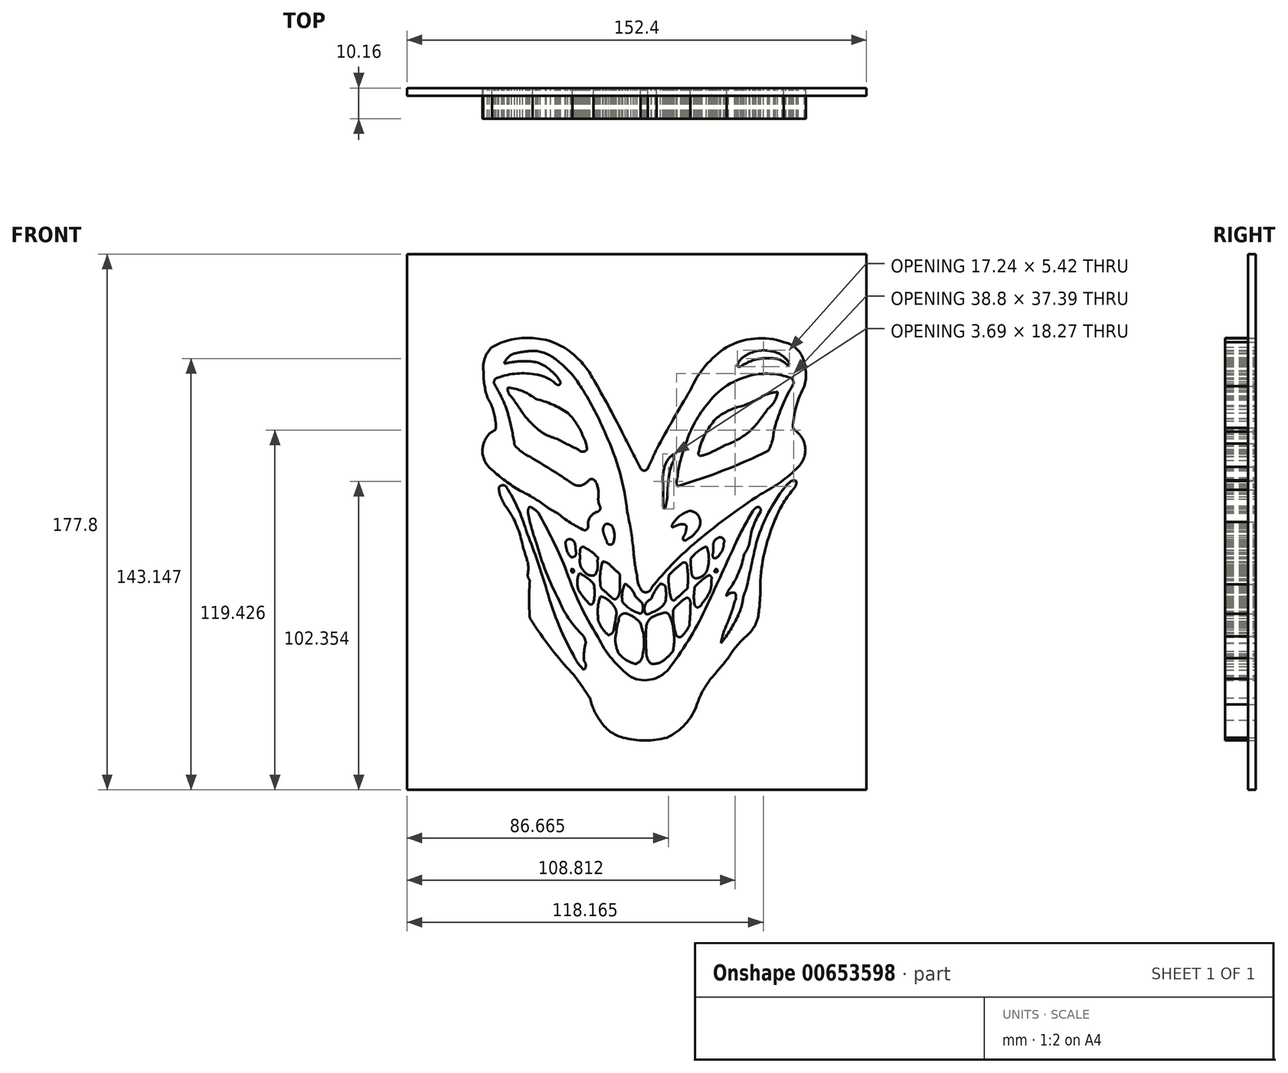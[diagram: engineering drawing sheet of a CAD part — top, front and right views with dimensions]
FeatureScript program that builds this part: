
annotation { "Feature Type Name" : "Feature", "Feature Type Description" : "" }
export const myFeature = defineFeature(function(context is Context, id is Id, definition is map)
    precondition{}
    {
        {
            var Q0;
            Q0=qCreatedBy(makeId("Front.planeOp"),FACE);
            var sketch = newSketch(context, id + "F0", { "sketchPlane" : qUnion([Q0])});
            skArc(sketch, "E0", {"start": v(-41.53, -5.05) * mm, "mid": v(-43.41, 1.4) * mm, "end": v(-46.62, 7.33) * mm});
            skArc(sketch, "E1", {"start": v(-48.45, 10.4) * mm, "mid": v(-47.67, 8.78) * mm, "end": v(-46.62, 7.33) * mm});
            skArc(sketch, "E2", {"start": v(-49.37, 14.24) * mm, "mid": v(-49.18, 12.26) * mm, "end": v(-48.45, 10.4) * mm});
            skArc(sketch, "E3", {"start": v(-46.78, 14.24) * mm, "mid": v(-48.07, 14.96) * mm, "end": v(-49.37, 14.24) * mm});
            skArc(sketch, "E4", {"start": v(-40.37, 0) * mm, "mid": v(-43.1, 7.34) * mm, "end": v(-46.78, 14.24) * mm});
            skArc(sketch, "E5", {"start": v(-33.87, -18.5) * mm, "mid": v(-36.95, -9.2) * mm, "end": v(-40.37, 0) * mm});
            skArc(sketch, "E6", {"start": v(-33.87, -18.5) * mm, "mid": v(-29.97, -30.28) * mm, "end": v(-24.64, -41.48) * mm});
            skArc(sketch, "E7", {"start": v(-24.64, -41.48) * mm, "mid": v(-23.16, -44.1) * mm, "end": v(-21.16, -46.36) * mm});
            skArc(sketch, "E8", {"start": v(-21.16, -46.36) * mm, "mid": v(-20.57, -44.83) * mm, "end": v(-21.16, -43.3) * mm});
            skArc(sketch, "E9", {"start": v(-20.57, -37.35) * mm, "mid": v(-21.1, -40.3) * mm, "end": v(-21.16, -43.3) * mm});
            skPoint(sketch, "E9.startSnap0", {"position": v(-20.57, -44.83) * mm});
            skArc(sketch, "E10", {"start": v(-20.57, -37.35) * mm, "mid": v(-21.1, -35.6) * mm, "end": v(-22.25, -34.18) * mm});
            skArc(sketch, "E11", {"start": v(-29.38, -23.38) * mm, "mid": v(-26.34, -29.12) * mm, "end": v(-22.25, -34.18) * mm});
            skArc(sketch, "E12", {"start": v(-37.08, -3.88) * mm, "mid": v(-33.77, -13.84) * mm, "end": v(-29.38, -23.38) * mm});
            skArc(sketch, "E13", {"start": v(-39.67, 5.78) * mm, "mid": v(-38.6, 0.89) * mm, "end": v(-37.08, -3.88) * mm});
            skArc(sketch, "E14", {"start": v(-39.22, 7.8) * mm, "mid": v(-39.7, 6.84) * mm, "end": v(-39.67, 5.78) * mm});
            skArc(sketch, "E15", {"start": v(-36.3, 5.78) * mm, "mid": v(-37.62, 6.98) * mm, "end": v(-39.22, 7.8) * mm});
            skArc(sketch, "E16", {"start": v(-27.4, -12.3) * mm, "mid": v(-31.6, -3.14) * mm, "end": v(-36.3, 5.78) * mm});
            skArc(sketch, "E17", {"start": v(-27.4, -12.3) * mm, "mid": v(-22.67, -24.21) * mm, "end": v(-16.52, -35.45) * mm});
            skArc(sketch, "E18", {"start": v(-16.52, -35.45) * mm, "mid": v(-11.84, -42.77) * mm, "end": v(-5.52, -48.73) * mm});
            skArc(sketch, "E19", {"start": v(-5.52, -48.73) * mm, "mid": v(1.65, -49.42) * mm, "end": v(7.53, -45.26) * mm});
            skArc(sketch, "E20", {"start": v(7.53, -45.26) * mm, "mid": v(14.21, -35.37) * mm, "end": v(19.76, -24.8) * mm});
            skArc(sketch, "E21", {"start": v(19.76, -24.8) * mm, "mid": v(24.58, -14.35) * mm, "end": v(29.35, -3.88) * mm});
            skArc(sketch, "E22", {"start": v(34.83, 6.26) * mm, "mid": v(31.93, 1.27) * mm, "end": v(29.35, -3.88) * mm});
            skArc(sketch, "E23", {"start": v(36.8, 7.8) * mm, "mid": v(35.63, 7.26) * mm, "end": v(34.83, 6.26) * mm});
            skArc(sketch, "E24", {"start": v(37.5, 6.26) * mm, "mid": v(37.4, 7.14) * mm, "end": v(36.8, 7.8) * mm});
            skArc(sketch, "E25", {"start": v(37.5, 6.26) * mm, "mid": v(34.94, 1.1) * mm, "end": v(33.71, -4.53) * mm});
            skArc(sketch, "E26", {"start": v(31.96, -7.9) * mm, "mid": v(32.99, -6.29) * mm, "end": v(33.71, -4.53) * mm});
            skArc(sketch, "E27", {"start": v(26.85, -19.87) * mm, "mid": v(30.12, -14.19) * mm, "end": v(31.96, -7.9) * mm});
            skArc(sketch, "E28", {"start": v(26.85, -19.87) * mm, "mid": v(26.35, -20.88) * mm, "end": v(25.97, -21.94) * mm});
            skArc(sketch, "E29", {"start": v(28.92, -20.7) * mm, "mid": v(27.28, -20.92) * mm, "end": v(25.97, -21.94) * mm});
            skArc(sketch, "E30", {"start": v(28.92, -23.62) * mm, "mid": v(29.3, -22.16) * mm, "end": v(28.92, -20.7) * mm});
            skArc(sketch, "E31", {"start": v(26.29, -31.16) * mm, "mid": v(27.72, -27.43) * mm, "end": v(28.92, -23.62) * mm});
            skArc(sketch, "E32", {"start": v(26.29, -31.16) * mm, "mid": v(25.07, -34.27) * mm, "end": v(24.29, -37.52) * mm});
            skArc(sketch, "E33", {"start": v(24.29, -37.52) * mm, "mid": v(27.43, -33) * mm, "end": v(30.06, -28.15) * mm});
            skArc(sketch, "E34", {"start": v(30.06, -28.15) * mm, "mid": v(30.9, -25.93) * mm, "end": v(31.48, -23.62) * mm});
            skArc(sketch, "E35", {"start": v(32.71, -19.43) * mm, "mid": v(31.9, -21.47) * mm, "end": v(31.48, -23.62) * mm});
            skArc(sketch, "E36", {"start": v(36.02, -4.21) * mm, "mid": v(34.34, -11.82) * mm, "end": v(32.71, -19.43) * mm});
            skArc(sketch, "E37", {"start": v(44.6, 13.13) * mm, "mid": v(39.53, 4.84) * mm, "end": v(36.02, -4.21) * mm});
            skArc(sketch, "E38", {"start": v(47.58, 16.36) * mm, "mid": v(45.99, 14.84) * mm, "end": v(44.6, 13.13) * mm});
            skArc(sketch, "E39", {"start": v(49.32, 16.36) * mm, "mid": v(48.45, 16.56) * mm, "end": v(47.58, 16.36) * mm});
            skArc(sketch, "E40", {"start": v(48.2, 13.49) * mm, "mid": v(49.07, 14.8) * mm, "end": v(49.32, 16.36) * mm});
            skArc(sketch, "E41", {"start": v(48.2, 13.49) * mm, "mid": v(44.6, 8.4) * mm, "end": v(41.97, 2.74) * mm});
            skArc(sketch, "E42", {"start": v(41.97, 2.74) * mm, "mid": v(38.7, -7.4) * mm, "end": v(37.36, -17.96) * mm});
            skArc(sketch, "E43", {"start": v(36.75, -27.73) * mm, "mid": v(37.25, -22.86) * mm, "end": v(37.36, -17.96) * mm});
            skArc(sketch, "E44", {"start": v(32.61, -35.23) * mm, "mid": v(35.4, -31.88) * mm, "end": v(36.75, -27.73) * mm});
            skArc(sketch, "E45", {"start": v(32.61, -35.23) * mm, "mid": v(29.35, -38.6) * mm, "end": v(26.66, -42.44) * mm});
            skArc(sketch, "E46", {"start": v(20.89, -49.35) * mm, "mid": v(23.8, -45.91) * mm, "end": v(26.66, -42.44) * mm});
            skArc(sketch, "E47", {"start": v(20.89, -49.35) * mm, "mid": v(18.24, -53.39) * mm, "end": v(16.34, -57.82) * mm});
            skArc(sketch, "E48", {"start": v(6.39, -68.82) * mm, "mid": v(12.47, -64.32) * mm, "end": v(16.34, -57.82) * mm});
            skArc(sketch, "E49", {"start": v(-8.19, -68.82) * mm, "mid": v(-0.9, -69.82) * mm, "end": v(6.39, -68.82) * mm});
            skArc(sketch, "E50", {"start": v(-15.9, -63) * mm, "mid": v(-12.62, -66.68) * mm, "end": v(-8.19, -68.82) * mm});
            skArc(sketch, "E51", {"start": v(-19.19, -55.72) * mm, "mid": v(-17.92, -59.54) * mm, "end": v(-15.9, -63) * mm});
            skArc(sketch, "E52", {"start": v(-19.19, -55.72) * mm, "mid": v(-21.73, -51.9) * mm, "end": v(-24.41, -48.18) * mm});
            skArc(sketch, "E53", {"start": v(-37, -32.37) * mm, "mid": v(-31.05, -40.54) * mm, "end": v(-24.41, -48.18) * mm});
            skArc(sketch, "E54", {"start": v(-37, -32.37) * mm, "mid": v(-38.03, -30.76) * mm, "end": v(-39.12, -29.2) * mm});
            skArc(sketch, "E55", {"start": v(-39.12, -16.6) * mm, "mid": v(-39.34, -22.9) * mm, "end": v(-39.12, -29.2) * mm});
            skArc(sketch, "E56", {"start": v(-39.84, -14.65) * mm, "mid": v(-39.7, -15.7) * mm, "end": v(-39.12, -16.6) * mm});
            skArc(sketch, "E57", {"start": v(-39.84, -14.65) * mm, "mid": v(-39.63, -12.58) * mm, "end": v(-39.84, -10.51) * mm});
            skArc(sketch, "E58", {"start": v(-41.53, -5.05) * mm, "mid": v(-40.7, -7.78) * mm, "end": v(-39.84, -10.51) * mm});
            skSolve(sketch);
        }
        {
            var Q0;
            Q0=makeQuery(id+"F0.imprint","IMPRINT",FACE,{"disambiguationData":[TD([[makeQuery(id+"F0.imprint","IMPRINT",EDGE,{"derivedFrom":sQuery(id+"F0.wireOp",EDGE,"E0")}),-1.0]])]});
            extrude(context, id + "F1", {"entities" : qUnion([Q0]), "depth" : 10.16 * mm, "offsetDistance" : 25.4 * mm});
        }
        {
            var Q0;
            Q0=qCreatedBy(makeId("Front.planeOp"),FACE);
            var sketch = newSketch(context, id + "F2", { "sketchPlane" : qUnion([Q0])});
            skArc(sketch, "E59", {"start": v(-24.05, -4.96) * mm, "mid": v(-24.52, -3.7) * mm, "end": v(-25.64, -2.96) * mm});
            skArc(sketch, "E60", {"start": v(-25.64, -2.96) * mm, "mid": v(-27, -3.46) * mm, "end": v(-27.17, -4.9) * mm});
            skArc(sketch, "E61", {"start": v(-27.17, -4.9) * mm, "mid": v(-26.72, -6.97) * mm, "end": v(-25.64, -8.8) * mm});
            skArc(sketch, "E62", {"start": v(-25.64, -8.8) * mm, "mid": v(-24.23, -8.62) * mm, "end": v(-23.81, -7.26) * mm});
            skArc(sketch, "E63", {"start": v(-24.05, -4.96) * mm, "mid": v(-23.95, -6.11) * mm, "end": v(-23.81, -7.26) * mm});
            skArc(sketch, "E64", {"start": v(-16.42, -9.3) * mm, "mid": v(-18.7, -7.09) * mm, "end": v(-21.46, -5.5) * mm});
            skArc(sketch, "E65", {"start": v(-16.42, -9.3) * mm, "mid": v(-16.64, -9.79) * mm, "end": v(-16.71, -10.32) * mm});
            skArc(sketch, "E66", {"start": v(-17.54, -14.86) * mm, "mid": v(-16.66, -12.68) * mm, "end": v(-16.71, -10.32) * mm});
            skArc(sketch, "E67", {"start": v(-21.13, -13.62) * mm, "mid": v(-19.55, -14.86) * mm, "end": v(-17.54, -14.86) * mm});
            skArc(sketch, "E68", {"start": v(-22.42, -9.14) * mm, "mid": v(-22.37, -11.56) * mm, "end": v(-21.13, -13.62) * mm});
            skArc(sketch, "E69", {"start": v(-22.42, -6.64) * mm, "mid": v(-22.53, -7.9) * mm, "end": v(-22.42, -9.14) * mm});
            skArc(sketch, "E70", {"start": v(-21.46, -5.5) * mm, "mid": v(-22.2, -5.85) * mm, "end": v(-22.42, -6.64) * mm});
            skArc(sketch, "E71", {"start": v(-12.3, -11.8) * mm, "mid": v(-13.48, -10.82) * mm, "end": v(-14.93, -10.34) * mm});
            skArc(sketch, "E72", {"start": v(-14.93, -10.34) * mm, "mid": v(-15.73, -14) * mm, "end": v(-15.7, -17.73) * mm});
            skArc(sketch, "E73", {"start": v(-15.7, -17.73) * mm, "mid": v(-15.56, -18.83) * mm, "end": v(-14.93, -19.73) * mm});
            skArc(sketch, "E74", {"start": v(-12.05, -22.32) * mm, "mid": v(-13.45, -20.99) * mm, "end": v(-14.93, -19.73) * mm});
            skArc(sketch, "E75", {"start": v(-12.05, -22.32) * mm, "mid": v(-11.3, -22.82) * mm, "end": v(-10.4, -22.79) * mm});
            skArc(sketch, "E76", {"start": v(-10.4, -22.79) * mm, "mid": v(-9.38, -20.82) * mm, "end": v(-9.27, -18.6) * mm});
            skArc(sketch, "E77", {"start": v(-9.27, -18.6) * mm, "mid": v(-9.25, -16.84) * mm, "end": v(-9.27, -15.09) * mm});
            skArc(sketch, "E78", {"start": v(-9.27, -15.09) * mm, "mid": v(-9.34, -14.6) * mm, "end": v(-9.64, -14.21) * mm});
            skArc(sketch, "E79", {"start": v(-12.3, -11.8) * mm, "mid": v(-10.99, -13.02) * mm, "end": v(-9.64, -14.21) * mm});
            skArc(sketch, "E80", {"start": v(-17.97, -17.73) * mm, "mid": v(-20.2, -15.74) * mm, "end": v(-22.76, -14.21) * mm});
            skArc(sketch, "E81", {"start": v(-17.97, -23.83) * mm, "mid": v(-17.6, -20.78) * mm, "end": v(-17.97, -17.73) * mm});
            skArc(sketch, "E82", {"start": v(-19.3, -24.54) * mm, "mid": v(-18.46, -24.52) * mm, "end": v(-17.97, -23.83) * mm});
            skArc(sketch, "E83", {"start": v(-23.05, -19.73) * mm, "mid": v(-21.3, -22.24) * mm, "end": v(-19.3, -24.54) * mm});
            skArc(sketch, "E84", {"start": v(-22.76, -14.21) * mm, "mid": v(-23.37, -16.95) * mm, "end": v(-23.05, -19.73) * mm});
            skArc(sketch, "E85", {"start": v(-24.45, -13.41) * mm, "mid": v(-24.75, -12.96) * mm, "end": v(-25.29, -12.88) * mm});
            skArc(sketch, "E86", {"start": v(-24.65, -14) * mm, "mid": v(-24.48, -13.73) * mm, "end": v(-24.45, -13.41) * mm});
            skArc(sketch, "E87", {"start": v(-25.28, -13.74) * mm, "mid": v(-25.01, -14) * mm, "end": v(-24.65, -14) * mm});
            skArc(sketch, "E88", {"start": v(-25.29, -12.88) * mm, "mid": v(-25.42, -13.31) * mm, "end": v(-25.28, -13.74) * mm});
            skArc(sketch, "E89", {"start": v(-4.2, -21.86) * mm, "mid": v(-5.47, -19.49) * mm, "end": v(-7.52, -17.73) * mm});
            skArc(sketch, "E90", {"start": v(-4.2, -21.86) * mm, "mid": v(-3.2, -22.91) * mm, "end": v(-2.07, -23.83) * mm});
            skArc(sketch, "E91", {"start": v(-1.72, -26.77) * mm, "mid": v(-1.58, -25.27) * mm, "end": v(-2.07, -23.83) * mm});
            skArc(sketch, "E92", {"start": v(-2.57, -27.66) * mm, "mid": v(-1.95, -27.4) * mm, "end": v(-1.72, -26.77) * mm});
            skArc(sketch, "E93", {"start": v(-8.36, -23.83) * mm, "mid": v(-5.75, -26.18) * mm, "end": v(-2.57, -27.66) * mm});
            skArc(sketch, "E94", {"start": v(-7.52, -17.73) * mm, "mid": v(-8.47, -20.7) * mm, "end": v(-8.36, -23.83) * mm});
            skArc(sketch, "E95", {"start": v(-15.7, -21.95) * mm, "mid": v(-16.48, -25.13) * mm, "end": v(-16.52, -28.4) * mm});
            skArc(sketch, "E96", {"start": v(-16.52, -28.4) * mm, "mid": v(-16.4, -30.03) * mm, "end": v(-15.7, -31.51) * mm});
            skArc(sketch, "E97", {"start": v(-15.7, -31.51) * mm, "mid": v(-14.52, -33.35) * mm, "end": v(-12.91, -34.83) * mm});
            skArc(sketch, "E98", {"start": v(-12.91, -34.83) * mm, "mid": v(-11.87, -34.17) * mm, "end": v(-11.28, -33.1) * mm});
            skArc(sketch, "E99", {"start": v(-11.28, -33.1) * mm, "mid": v(-10.8, -30.38) * mm, "end": v(-10.4, -27.66) * mm});
            skArc(sketch, "E100", {"start": v(-10.4, -27.66) * mm, "mid": v(-10.6, -26.3) * mm, "end": v(-11.28, -25.12) * mm});
            skArc(sketch, "E101", {"start": v(-11.28, -25.12) * mm, "mid": v(-13.17, -23.1) * mm, "end": v(-15.7, -21.95) * mm});
            skArc(sketch, "E102", {"start": v(-6.46, -27.86) * mm, "mid": v(-8.78, -28) * mm, "end": v(-9.64, -30.15) * mm});
            skArc(sketch, "E103", {"start": v(-2.57, -30.64) * mm, "mid": v(-4.36, -29.03) * mm, "end": v(-6.46, -27.86) * mm});
            skArc(sketch, "E104", {"start": v(-1.72, -41.64) * mm, "mid": v(-1.27, -36.08) * mm, "end": v(-2.57, -30.64) * mm});
            skArc(sketch, "E105", {"start": v(-4.2, -44.37) * mm, "mid": v(-2.5, -43.43) * mm, "end": v(-1.72, -41.64) * mm});
            skArc(sketch, "E106", {"start": v(-9.64, -40.87) * mm, "mid": v(-7.18, -43.04) * mm, "end": v(-4.2, -44.37) * mm});
            skArc(sketch, "E107", {"start": v(-10.4, -33.87) * mm, "mid": v(-10.69, -37.44) * mm, "end": v(-9.64, -40.87) * mm});
            skArc(sketch, "E108", {"start": v(-9.64, -30.15) * mm, "mid": v(-10.19, -31.97) * mm, "end": v(-10.4, -33.87) * mm});
            skArc(sketch, "E109", {"start": v(1.1, -22.79) * mm, "mid": v(0, -23.5) * mm, "end": v(-0.77, -24.54) * mm});
            skArc(sketch, "E110", {"start": v(4.18, -17.73) * mm, "mid": v(2.42, -20.12) * mm, "end": v(1.1, -22.79) * mm});
            skArc(sketch, "E111", {"start": v(5.84, -18.6) * mm, "mid": v(5.1, -17.99) * mm, "end": v(4.18, -17.73) * mm});
            skArc(sketch, "E112", {"start": v(5.84, -23.83) * mm, "mid": v(6.1, -21.22) * mm, "end": v(5.84, -18.6) * mm});
            skArc(sketch, "E113", {"start": v(1.1, -27.29) * mm, "mid": v(3.82, -26.03) * mm, "end": v(5.84, -23.83) * mm});
            skArc(sketch, "E114", {"start": v(-0.65, -27.86) * mm, "mid": v(0.31, -27.83) * mm, "end": v(1.1, -27.29) * mm});
            skArc(sketch, "E115", {"start": v(-0.77, -24.54) * mm, "mid": v(-1.13, -26.22) * mm, "end": v(-0.65, -27.86) * mm});
            skArc(sketch, "E116", {"start": v(2.47, -28.4) * mm, "mid": v(0.46, -29.73) * mm, "end": v(-0.5, -31.94) * mm});
            skArc(sketch, "E117", {"start": v(-0.5, -31.94) * mm, "mid": v(-0.68, -36.03) * mm, "end": v(-0.5, -40.12) * mm});
            skArc(sketch, "E118", {"start": v(-0.5, -40.12) * mm, "mid": v(-0.16, -42.43) * mm, "end": v(1.1, -44.37) * mm});
            skArc(sketch, "E119", {"start": v(1.1, -44.37) * mm, "mid": v(3.66, -44.04) * mm, "end": v(5.84, -42.68) * mm});
            skArc(sketch, "E120", {"start": v(5.84, -42.68) * mm, "mid": v(7.2, -41.5) * mm, "end": v(8.36, -40.12) * mm});
            skArc(sketch, "E121", {"start": v(8.36, -40.12) * mm, "mid": v(8.76, -37.02) * mm, "end": v(8.6, -33.89) * mm});
            skArc(sketch, "E122", {"start": v(8.6, -33.89) * mm, "mid": v(8.2, -31.08) * mm, "end": v(7.28, -28.4) * mm});
            skArc(sketch, "E123", {"start": v(7.28, -28.4) * mm, "mid": v(6.7, -27.66) * mm, "end": v(5.84, -27.29) * mm});
            skArc(sketch, "E124", {"start": v(5.84, -27.29) * mm, "mid": v(4.12, -27.73) * mm, "end": v(2.47, -28.4) * mm});
            skArc(sketch, "E125", {"start": v(9.83, -24.9) * mm, "mid": v(8.89, -25.77) * mm, "end": v(8.36, -26.94) * mm});
            skArc(sketch, "E126", {"start": v(8.36, -26.94) * mm, "mid": v(8.57, -30.93) * mm, "end": v(9.44, -34.83) * mm});
            skArc(sketch, "E127", {"start": v(9.44, -34.83) * mm, "mid": v(10.42, -35.47) * mm, "end": v(11.5, -35.01) * mm});
            skArc(sketch, "E128", {"start": v(11.5, -35.01) * mm, "mid": v(12.8, -33.36) * mm, "end": v(13.82, -31.51) * mm});
            skArc(sketch, "E129", {"start": v(13.82, -31.51) * mm, "mid": v(14.06, -28.03) * mm, "end": v(14.19, -24.54) * mm});
            skArc(sketch, "E130", {"start": v(14.19, -24.54) * mm, "mid": v(14.1, -23.51) * mm, "end": v(13.58, -22.61) * mm});
            skArc(sketch, "E131", {"start": v(13.58, -22.61) * mm, "mid": v(13.1, -22.41) * mm, "end": v(12.6, -22.61) * mm});
            skArc(sketch, "E132", {"start": v(12.6, -22.61) * mm, "mid": v(11.72, -23.13) * mm, "end": v(10.96, -23.8) * mm});
            skArc(sketch, "E133", {"start": v(10.96, -23.8) * mm, "mid": v(10.38, -24.33) * mm, "end": v(9.83, -24.9) * mm});
            skArc(sketch, "E134", {"start": v(7, -14.96) * mm, "mid": v(7.04, -18.82) * mm, "end": v(7.77, -22.61) * mm});
            skArc(sketch, "E135", {"start": v(7.77, -22.61) * mm, "mid": v(8.57, -23.26) * mm, "end": v(9.38, -22.61) * mm});
            skArc(sketch, "E136", {"start": v(9.38, -22.61) * mm, "mid": v(10.7, -21.6) * mm, "end": v(11.87, -20.42) * mm});
            skArc(sketch, "E137", {"start": v(11.87, -20.42) * mm, "mid": v(12.5, -19.89) * mm, "end": v(13.13, -19.34) * mm});
            skArc(sketch, "E138", {"start": v(13.13, -19.34) * mm, "mid": v(13.37, -16) * mm, "end": v(13.13, -12.68) * mm});
            skArc(sketch, "E139", {"start": v(13.13, -12.68) * mm, "mid": v(13.05, -11.65) * mm, "end": v(12.6, -10.72) * mm});
            skArc(sketch, "E140", {"start": v(12.6, -10.72) * mm, "mid": v(11.69, -10.75) * mm, "end": v(10.96, -11.3) * mm});
            skArc(sketch, "E141", {"start": v(10.96, -11.3) * mm, "mid": v(8.87, -13.02) * mm, "end": v(7, -14.96) * mm});
            skArc(sketch, "E142", {"start": v(19.5, -5.35) * mm, "mid": v(16.6, -7.02) * mm, "end": v(14.29, -9.41) * mm});
            skArc(sketch, "E143", {"start": v(19.5, -13.72) * mm, "mid": v(20.28, -9.54) * mm, "end": v(19.5, -5.35) * mm});
            skArc(sketch, "E144", {"start": v(15.97, -16) * mm, "mid": v(18.01, -15.3) * mm, "end": v(19.5, -13.72) * mm});
            skArc(sketch, "E145", {"start": v(14.54, -14.22) * mm, "mid": v(14.94, -15.36) * mm, "end": v(15.97, -16) * mm});
            skArc(sketch, "E146", {"start": v(14.29, -9.41) * mm, "mid": v(14.3, -11.82) * mm, "end": v(14.54, -14.22) * mm});
            skArc(sketch, "E147", {"start": v(23.8, -2.38) * mm, "mid": v(22.3, -3.3) * mm, "end": v(21.67, -4.96) * mm});
            skArc(sketch, "E148", {"start": v(25.19, -4.36) * mm, "mid": v(25.14, -2.92) * mm, "end": v(23.8, -2.38) * mm});
            skArc(sketch, "E149", {"start": v(24.15, -7.58) * mm, "mid": v(24.98, -6.07) * mm, "end": v(25.19, -4.36) * mm});
            skArc(sketch, "E150", {"start": v(22.12, -9.41) * mm, "mid": v(23.34, -8.72) * mm, "end": v(24.15, -7.58) * mm});
            skArc(sketch, "E151", {"start": v(21.67, -7.58) * mm, "mid": v(21.57, -8.58) * mm, "end": v(22.12, -9.41) * mm});
            skArc(sketch, "E152", {"start": v(21.67, -7.58) * mm, "mid": v(21.7, -6.27) * mm, "end": v(21.67, -4.96) * mm});
            skArc(sketch, "E153", {"start": v(22.35, -13.33) * mm, "mid": v(22.18, -13.4) * mm, "end": v(22.12, -13.57) * mm});
            skArc(sketch, "E154", {"start": v(22.6, -12.86) * mm, "mid": v(22.4, -13.06) * mm, "end": v(22.35, -13.33) * mm});
            skArc(sketch, "E155", {"start": v(23.04, -13.12) * mm, "mid": v(22.9, -12.86) * mm, "end": v(22.6, -12.86) * mm});
            skArc(sketch, "E156", {"start": v(23.04, -13.84) * mm, "mid": v(23.1, -13.48) * mm, "end": v(23.04, -13.12) * mm});
            skArc(sketch, "E157", {"start": v(22.34, -13.84) * mm, "mid": v(22.69, -13.95) * mm, "end": v(23.04, -13.84) * mm});
            skArc(sketch, "E158", {"start": v(22.12, -13.57) * mm, "mid": v(22.18, -13.75) * mm, "end": v(22.34, -13.84) * mm});
            skArc(sketch, "E159", {"start": v(15.64, -18.76) * mm, "mid": v(15.32, -21.58) * mm, "end": v(15.47, -24.41) * mm});
            skArc(sketch, "E160", {"start": v(20.27, -14.9) * mm, "mid": v(17.8, -16.66) * mm, "end": v(15.64, -18.76) * mm});
            skArc(sketch, "E161", {"start": v(21.12, -16.38) * mm, "mid": v(21.07, -15.43) * mm, "end": v(20.27, -14.9) * mm});
            skArc(sketch, "E162", {"start": v(20.86, -19.74) * mm, "mid": v(21.1, -18.07) * mm, "end": v(21.12, -16.38) * mm});
            skArc(sketch, "E163", {"start": v(18.11, -24.2) * mm, "mid": v(19.66, -22.08) * mm, "end": v(20.86, -19.74) * mm});
            skArc(sketch, "E164", {"start": v(16.53, -25.67) * mm, "mid": v(17.47, -25.1) * mm, "end": v(18.11, -24.2) * mm});
            skArc(sketch, "E165", {"start": v(15.47, -24.41) * mm, "mid": v(15.82, -25.19) * mm, "end": v(16.53, -25.67) * mm});
            skArc(sketch, "E166", {"start": v(-14.12, 2.04) * mm, "mid": v(-14.74, 0.85) * mm, "end": v(-14.77, -0.49) * mm});
            skArc(sketch, "E167", {"start": v(-11.55, 0.75) * mm, "mid": v(-12.57, 1.93) * mm, "end": v(-14.12, 2.04) * mm});
            skArc(sketch, "E168", {"start": v(-11.55, -4.36) * mm, "mid": v(-11.05, -1.8) * mm, "end": v(-11.55, 0.75) * mm});
            skArc(sketch, "E169", {"start": v(-13.63, -3.56) * mm, "mid": v(-12.87, -4.7) * mm, "end": v(-11.55, -4.36) * mm});
            skArc(sketch, "E170", {"start": v(-14.77, -0.49) * mm, "mid": v(-14.27, -2.05) * mm, "end": v(-13.63, -3.56) * mm});
            skSolve(sketch);
        }
        {
            var Q0;
            Q0=makeQuery(id+"F2.imprint","IMPRINT",FACE,{"disambiguationData":[TD([[makeQuery(id+"F2.imprint","IMPRINT",EDGE,{"derivedFrom":sQuery(id+"F2.wireOp",EDGE,"E59")}),1.0]])]});
            var Q1;
            Q1=makeQuery(id+"F2.imprint","IMPRINT",FACE,{"disambiguationData":[TD([[makeQuery(id+"F2.imprint","IMPRINT",EDGE,{"derivedFrom":sQuery(id+"F2.wireOp",EDGE,"E64")}),1.0]])]});
            var Q2;
            Q2=makeQuery(id+"F2.imprint","IMPRINT",FACE,{"disambiguationData":[TD([[makeQuery(id+"F2.imprint","IMPRINT",EDGE,{"derivedFrom":sQuery(id+"F2.wireOp",EDGE,"E166")}),1.0]])]});
            var Q3;
            Q3=makeQuery(id+"F2.imprint","IMPRINT",FACE,{"disambiguationData":[TD([[makeQuery(id+"F2.imprint","IMPRINT",EDGE,{"derivedFrom":sQuery(id+"F2.wireOp",EDGE,"E71")}),1.0]])]});
            var Q4;
            Q4=makeQuery(id+"F2.imprint","IMPRINT",FACE,{"disambiguationData":[TD([[makeQuery(id+"F2.imprint","IMPRINT",EDGE,{"derivedFrom":sQuery(id+"F2.wireOp",EDGE,"E80")}),1.0]])]});
            var Q5;
            Q5=makeQuery(id+"F2.imprint","IMPRINT",FACE,{"disambiguationData":[TD([[makeQuery(id+"F2.imprint","IMPRINT",EDGE,{"derivedFrom":sQuery(id+"F2.wireOp",EDGE,"E85")}),1.0]])]});
            var Q6;
            Q6=makeQuery(id+"F2.imprint","IMPRINT",FACE,{"disambiguationData":[TD([[makeQuery(id+"F2.imprint","IMPRINT",EDGE,{"derivedFrom":sQuery(id+"F2.wireOp",EDGE,"E95")}),1.0]])]});
            var Q7;
            Q7=makeQuery(id+"F2.imprint","IMPRINT",FACE,{"disambiguationData":[TD([[makeQuery(id+"F2.imprint","IMPRINT",EDGE,{"derivedFrom":sQuery(id+"F2.wireOp",EDGE,"E89")}),1.0]])]});
            var Q8;
            Q8=makeQuery(id+"F2.imprint","IMPRINT",FACE,{"disambiguationData":[TD([[makeQuery(id+"F2.imprint","IMPRINT",EDGE,{"derivedFrom":sQuery(id+"F2.wireOp",EDGE,"E102")}),1.0]])]});
            var Q9;
            Q9=makeQuery(id+"F2.imprint","IMPRINT",FACE,{"disambiguationData":[TD([[makeQuery(id+"F2.imprint","IMPRINT",EDGE,{"derivedFrom":sQuery(id+"F2.wireOp",EDGE,"E116")}),1.0]])]});
            var Q10;
            Q10=makeQuery(id+"F2.imprint","IMPRINT",FACE,{"disambiguationData":[TD([[makeQuery(id+"F2.imprint","IMPRINT",EDGE,{"derivedFrom":sQuery(id+"F2.wireOp",EDGE,"E109")}),1.0]])]});
            var Q11;
            Q11=makeQuery(id+"F2.imprint","IMPRINT",FACE,{"disambiguationData":[TD([[makeQuery(id+"F2.imprint","IMPRINT",EDGE,{"derivedFrom":sQuery(id+"F2.wireOp",EDGE,"E125")}),1.0]])]});
            var Q12;
            Q12=makeQuery(id+"F2.imprint","IMPRINT",FACE,{"disambiguationData":[TD([[makeQuery(id+"F2.imprint","IMPRINT",EDGE,{"derivedFrom":sQuery(id+"F2.wireOp",EDGE,"E134")}),1.0]])]});
            var Q13;
            Q13=makeQuery(id+"F2.imprint","IMPRINT",FACE,{"disambiguationData":[TD([[makeQuery(id+"F2.imprint","IMPRINT",EDGE,{"derivedFrom":sQuery(id+"F2.wireOp",EDGE,"E159")}),1.0]])]});
            var Q14;
            Q14=makeQuery(id+"F2.imprint","IMPRINT",FACE,{"disambiguationData":[TD([[makeQuery(id+"F2.imprint","IMPRINT",EDGE,{"derivedFrom":sQuery(id+"F2.wireOp",EDGE,"E142")}),1.0]])]});
            var Q15;
            Q15=makeQuery(id+"F2.imprint","IMPRINT",FACE,{"disambiguationData":[TD([[makeQuery(id+"F2.imprint","IMPRINT",EDGE,{"derivedFrom":sQuery(id+"F2.wireOp",EDGE,"E147")}),1.0]])]});
            var Q16;
            Q16=makeQuery(id+"F2.imprint","IMPRINT",FACE,{"disambiguationData":[TD([[makeQuery(id+"F2.imprint","IMPRINT",EDGE,{"derivedFrom":sQuery(id+"F2.wireOp",EDGE,"E153")}),1.0]])]});
            extrude(context, id + "F3", {"entities" : qUnion([Q0, Q1, Q2, Q3, Q4, Q5, Q6, Q7, Q8, Q9, Q10, Q11, Q12, Q13, Q14, Q15, Q16]), "depth" : 10.16 * mm, "offsetDistance" : 25.4 * mm});
        }
        {
            var Q0;
            Q0=qCreatedBy(makeId("Front.planeOp"),FACE);
            var sketch = newSketch(context, id + "F4", { "sketchPlane" : qUnion([Q0])});
            skArc(sketch, "E171", {"start": v(-29.98, 5.72) * mm, "mid": v(-25.69, 2.53) * mm, "end": v(-20.98, 0) * mm});
            skArc(sketch, "E172", {"start": v(-20.98, 0) * mm, "mid": v(-20.1, 0.42) * mm, "end": v(-19.8, 1.35) * mm});
            skArc(sketch, "E173", {"start": v(-17, 6.05) * mm, "mid": v(-19.23, 4.2) * mm, "end": v(-19.8, 1.35) * mm});
            skArc(sketch, "E174", {"start": v(-17, 6.05) * mm, "mid": v(-15.99, 6.64) * mm, "end": v(-15.8, 7.8) * mm});
            skArc(sketch, "E175", {"start": v(-16.37, 11.18) * mm, "mid": v(-16.36, 9.44) * mm, "end": v(-15.8, 7.8) * mm});
            skArc(sketch, "E176", {"start": v(-16.37, 11.18) * mm, "mid": v(-16.5, 13.96) * mm, "end": v(-17.54, 16.55) * mm});
            skArc(sketch, "E177", {"start": v(-17.54, 16.55) * mm, "mid": v(-18.36, 16.94) * mm, "end": v(-19.26, 16.89) * mm});
            skArc(sketch, "E178", {"start": v(-22.47, 14.8) * mm, "mid": v(-20.7, 15.58) * mm, "end": v(-19.26, 16.89) * mm});
            skArc(sketch, "E179", {"start": v(-25, 15.5) * mm, "mid": v(-23.8, 14.93) * mm, "end": v(-22.47, 14.8) * mm});
            skArc(sketch, "E180", {"start": v(-25, 15.5) * mm, "mid": v(-32, 20.09) * mm, "end": v(-39.13, 24.42) * mm});
            skArc(sketch, "E181", {"start": v(-44.18, 28.26) * mm, "mid": v(-41.86, 26.06) * mm, "end": v(-39.13, 24.42) * mm});
            skArc(sketch, "E182", {"start": v(-44.18, 28.26) * mm, "mid": v(-44.98, 32.72) * mm, "end": v(-45.98, 37.14) * mm});
            skArc(sketch, "E183", {"start": v(-45.98, 37.14) * mm, "mid": v(-46.86, 40.24) * mm, "end": v(-48.05, 43.24) * mm});
            skArc(sketch, "E184", {"start": v(-48.05, 43.24) * mm, "mid": v(-49.48, 46.03) * mm, "end": v(-51, 48.77) * mm});
            skArc(sketch, "E185", {"start": v(-49.82, 50.66) * mm, "mid": v(-50.77, 49.94) * mm, "end": v(-51, 48.77) * mm});
            skArc(sketch, "E186", {"start": v(-36.85, 51.66) * mm, "mid": v(-43.4, 52.03) * mm, "end": v(-49.82, 50.66) * mm});
            skArc(sketch, "E187", {"start": v(-30.73, 48.77) * mm, "mid": v(-33.57, 50.68) * mm, "end": v(-36.85, 51.66) * mm});
            skArc(sketch, "E188", {"start": v(-30.73, 48.77) * mm, "mid": v(-30.1, 48.35) * mm, "end": v(-29.34, 48.3) * mm});
            skArc(sketch, "E189", {"start": v(-29.34, 48.3) * mm, "mid": v(-29, 48.8) * mm, "end": v(-29.05, 49.4) * mm});
            skArc(sketch, "E190", {"start": v(-29.05, 49.4) * mm, "mid": v(-30.43, 51.38) * mm, "end": v(-32.19, 53.04) * mm});
            skArc(sketch, "E191", {"start": v(-32.19, 53.04) * mm, "mid": v(-34.85, 54.91) * mm, "end": v(-37.94, 55.98) * mm});
            skArc(sketch, "E192", {"start": v(-37.94, 55.98) * mm, "mid": v(-41.97, 56.1) * mm, "end": v(-45.98, 55.67) * mm});
            skArc(sketch, "E193", {"start": v(-47.6, 55.38) * mm, "mid": v(-46.79, 55.5) * mm, "end": v(-45.98, 55.67) * mm});
            skArc(sketch, "E194", {"start": v(-43.3, 58.86) * mm, "mid": v(-45.98, 57.77) * mm, "end": v(-47.6, 55.38) * mm});
            skArc(sketch, "E195", {"start": v(-36.85, 59.5) * mm, "mid": v(-40.1, 59.4) * mm, "end": v(-43.3, 58.86) * mm});
            skArc(sketch, "E196", {"start": v(-29.42, 55.82) * mm, "mid": v(-32.85, 58.24) * mm, "end": v(-36.85, 59.5) * mm});
            skArc(sketch, "E197", {"start": v(-21.9, 47.18) * mm, "mid": v(-25.27, 51.84) * mm, "end": v(-29.42, 55.82) * mm});
            skArc(sketch, "E198", {"start": v(-13.96, 31.82) * mm, "mid": v(-17.58, 39.68) * mm, "end": v(-21.9, 47.18) * mm});
            skArc(sketch, "E199", {"start": v(-6.8, 6.05) * mm, "mid": v(-9.29, 19.24) * mm, "end": v(-13.96, 31.82) * mm});
            skArc(sketch, "E200", {"start": v(-4.78, -6.5) * mm, "mid": v(-5.59, -0.19) * mm, "end": v(-6.8, 6.05) * mm});
            skArc(sketch, "E201", {"start": v(-4.78, -6.5) * mm, "mid": v(-4.33, -10.77) * mm, "end": v(-3.59, -15.01) * mm});
            skArc(sketch, "E202", {"start": v(-3.59, -15.01) * mm, "mid": v(-3.12, -17.78) * mm, "end": v(-1.8, -20.26) * mm});
            skArc(sketch, "E203", {"start": v(-1.8, -20.26) * mm, "mid": v(0.1, -20.44) * mm, "end": v(1.33, -18.99) * mm});
            skArc(sketch, "E204", {"start": v(15.25, -4.62) * mm, "mid": v(7.94, -11.47) * mm, "end": v(1.33, -18.99) * mm});
            skArc(sketch, "E205", {"start": v(37.48, 12) * mm, "mid": v(26.09, 4.05) * mm, "end": v(15.25, -4.62) * mm});
            skArc(sketch, "E206", {"start": v(37.48, 12) * mm, "mid": v(44.1, 16.02) * mm, "end": v(49.95, 21.09) * mm});
            skArc(sketch, "E207", {"start": v(49.95, 21.09) * mm, "mid": v(52.03, 24.66) * mm, "end": v(52.01, 28.79) * mm});
            skArc(sketch, "E208", {"start": v(52.01, 28.79) * mm, "mid": v(51, 30.92) * mm, "end": v(49.47, 32.73) * mm});
            skArc(sketch, "E209", {"start": v(48.13, 34.06) * mm, "mid": v(48.76, 33.36) * mm, "end": v(49.47, 32.73) * mm});
            skArc(sketch, "E210", {"start": v(52.01, 47.9) * mm, "mid": v(49.25, 41.21) * mm, "end": v(48.13, 34.06) * mm});
            skArc(sketch, "E211", {"start": v(52.01, 47.9) * mm, "mid": v(52.45, 52.61) * mm, "end": v(51.43, 57.23) * mm});
            skArc(sketch, "E212", {"start": v(51.43, 57.23) * mm, "mid": v(48.93, 60.68) * mm, "end": v(45.09, 62.49) * mm});
            skArc(sketch, "E213", {"start": v(45.09, 62.49) * mm, "mid": v(35.44, 63.65) * mm, "end": v(26.15, 60.77) * mm});
            skArc(sketch, "E214", {"start": v(26.15, 60.77) * mm, "mid": v(19.08, 54.53) * mm, "end": v(14.12, 46.5) * mm});
            skArc(sketch, "E215", {"start": v(14.12, 46.5) * mm, "mid": v(8.43, 36.78) * mm, "end": v(2.93, 26.95) * mm});
            skArc(sketch, "E216", {"start": v(0, 20.58) * mm, "mid": v(1.5, 23.75) * mm, "end": v(2.93, 26.95) * mm});
            skArc(sketch, "E217", {"start": v(-2.37, 20.58) * mm, "mid": v(-1.19, 19.82) * mm, "end": v(0, 20.58) * mm});
            skArc(sketch, "E218", {"start": v(-8.5, 32.48) * mm, "mid": v(-5.45, 26.52) * mm, "end": v(-2.37, 20.58) * mm});
            skArc(sketch, "E219", {"start": v(-8.5, 32.48) * mm, "mid": v(-13.11, 41.36) * mm, "end": v(-18.04, 50.08) * mm});
            skArc(sketch, "E220", {"start": v(-18.04, 50.08) * mm, "mid": v(-21.1, 54.72) * mm, "end": v(-25.01, 58.67) * mm});
            skArc(sketch, "E221", {"start": v(-25.01, 58.67) * mm, "mid": v(-31.21, 62.33) * mm, "end": v(-38.27, 63.8) * mm});
            skArc(sketch, "E222", {"start": v(-38.27, 63.8) * mm, "mid": v(-45.22, 63.28) * mm, "end": v(-51.72, 60.77) * mm});
            skArc(sketch, "E223", {"start": v(-51.72, 60.77) * mm, "mid": v(-54.07, 57.11) * mm, "end": v(-54.5, 52.8) * mm});
            skArc(sketch, "E224", {"start": v(-54.5, 52.8) * mm, "mid": v(-54.2, 48.33) * mm, "end": v(-53.16, 44) * mm});
            skArc(sketch, "E225", {"start": v(-50.56, 36.3) * mm, "mid": v(-51.43, 40.3) * mm, "end": v(-53.16, 44) * mm});
            skArc(sketch, "E226", {"start": v(-50.56, 33.32) * mm, "mid": v(-50.33, 34.81) * mm, "end": v(-50.56, 36.3) * mm});
            skArc(sketch, "E227", {"start": v(-50.56, 33.32) * mm, "mid": v(-51.6, 32.76) * mm, "end": v(-52.55, 32.07) * mm});
            skArc(sketch, "E228", {"start": v(-52.55, 32.07) * mm, "mid": v(-54.32, 29.15) * mm, "end": v(-54.83, 25.78) * mm});
            skArc(sketch, "E229", {"start": v(-54.83, 25.78) * mm, "mid": v(-53.88, 22.6) * mm, "end": v(-51.72, 20.08) * mm});
            skArc(sketch, "E230", {"start": v(-51.72, 20.08) * mm, "mid": v(-47.26, 16.4) * mm, "end": v(-42.45, 13.2) * mm});
            skArc(sketch, "E231", {"start": v(-33.58, 7.8) * mm, "mid": v(-37.86, 10.74) * mm, "end": v(-42.45, 13.2) * mm});
            skArc(sketch, "E232", {"start": v(-33.58, 7.8) * mm, "mid": v(-31.83, 6.67) * mm, "end": v(-29.98, 5.72) * mm});
            skSolve(sketch);
        }
        {
            var Q0;
            Q0=makeQuery(id+"F4.imprint","IMPRINT",FACE,{"disambiguationData":[TD([[makeQuery(id+"F4.imprint","IMPRINT",EDGE,{"derivedFrom":sQuery(id+"F4.wireOp",EDGE,"E171")}),1.0]])]});
            extrude(context, id + "F5", {"entities" : qUnion([Q0]), "depth" : 10.16 * mm, "offsetDistance" : 25.4 * mm});
        }
        {
            var Q0;
            Q0=qCreatedBy(makeId("Front.planeOp"),FACE);
            var sketch = newSketch(context, id + "F6", { "sketchPlane" : qUnion([Q0])});
            skArc(sketch, "E233", {"start": v(8.6, 23.17) * mm, "mid": v(7.43, 20.01) * mm, "end": v(6.9, 16.68) * mm});
            skArc(sketch, "E234", {"start": v(8.6, 23.17) * mm, "mid": v(8.67, 24.26) * mm, "end": v(8.6, 25.36) * mm});
            skArc(sketch, "E235", {"start": v(8.6, 25.36) * mm, "mid": v(6.8, 23.57) * mm, "end": v(5.63, 21.3) * mm});
            skArc(sketch, "E236", {"start": v(5.63, 21.3) * mm, "mid": v(5.04, 18.3) * mm, "end": v(5.08, 15.22) * mm});
            skArc(sketch, "E237", {"start": v(5.08, 8.12) * mm, "mid": v(5.14, 11.67) * mm, "end": v(5.08, 15.22) * mm});
            skArc(sketch, "E238", {"start": v(5.08, 8.12) * mm, "mid": v(5.26, 7.55) * mm, "end": v(5.63, 7.1) * mm});
            skArc(sketch, "E239", {"start": v(5.63, 7.1) * mm, "mid": v(6.3, 9.78) * mm, "end": v(6.56, 12.54) * mm});
            skArc(sketch, "E240", {"start": v(6.9, 16.68) * mm, "mid": v(6.7, 14.61) * mm, "end": v(6.56, 12.54) * mm});
            skArc(sketch, "E241", {"start": v(13.82, 6.4) * mm, "mid": v(10.47, 4.63) * mm, "end": v(8.08, 1.68) * mm});
            skArc(sketch, "E242", {"start": v(16.98, 4.48) * mm, "mid": v(15.68, 5.9) * mm, "end": v(13.82, 6.4) * mm});
            skArc(sketch, "E243", {"start": v(16.98, 0.8) * mm, "mid": v(17.42, 2.64) * mm, "end": v(16.98, 4.48) * mm});
            skArc(sketch, "E244", {"start": v(13.17, -2.93) * mm, "mid": v(15.35, -1.34) * mm, "end": v(16.98, 0.8) * mm});
            skArc(sketch, "E245", {"start": v(11.88, -3.38) * mm, "mid": v(12.59, -3.33) * mm, "end": v(13.17, -2.93) * mm});
            skArc(sketch, "E246", {"start": v(12.14, -1.75) * mm, "mid": v(11.71, -2.52) * mm, "end": v(11.88, -3.38) * mm});
            skArc(sketch, "E247", {"start": v(12.14, -1.75) * mm, "mid": v(12.56, -0.63) * mm, "end": v(12.78, 0.54) * mm});
            skArc(sketch, "E248", {"start": v(12.78, 0.54) * mm, "mid": v(12.84, 1.3) * mm, "end": v(12.33, 1.87) * mm});
            skArc(sketch, "E249", {"start": v(12.33, 1.87) * mm, "mid": v(11.04, 1.98) * mm, "end": v(9.78, 1.64) * mm});
            skArc(sketch, "E250", {"start": v(8.18, 0.98) * mm, "mid": v(8.98, 1.3) * mm, "end": v(9.78, 1.64) * mm});
            skArc(sketch, "E251", {"start": v(8.08, 1.68) * mm, "mid": v(7.98, 1.31) * mm, "end": v(8.18, 0.98) * mm});
            skArc(sketch, "E252", {"start": v(9.78, 14.6) * mm, "mid": v(25.1, 19.85) * mm, "end": v(39.93, 26.33) * mm});
            skArc(sketch, "E253", {"start": v(39.93, 26.33) * mm, "mid": v(41.23, 29.27) * mm, "end": v(41.75, 32.44) * mm});
            skArc(sketch, "E254", {"start": v(47.18, 46.6) * mm, "mid": v(43.98, 39.7) * mm, "end": v(41.75, 32.44) * mm});
            skArc(sketch, "E255", {"start": v(47.18, 46.6) * mm, "mid": v(47.8, 47.66) * mm, "end": v(48.35, 48.77) * mm});
            skArc(sketch, "E256", {"start": v(48.35, 48.77) * mm, "mid": v(48.13, 49.94) * mm, "end": v(47.18, 50.68) * mm});
            skArc(sketch, "E257", {"start": v(47.18, 50.68) * mm, "mid": v(41.28, 51.92) * mm, "end": v(35.25, 51.63) * mm});
            skArc(sketch, "E258", {"start": v(35.25, 51.63) * mm, "mid": v(26.36, 48.08) * mm, "end": v(19.44, 41.46) * mm});
            skArc(sketch, "E259", {"start": v(19.44, 41.46) * mm, "mid": v(15.21, 35.02) * mm, "end": v(12.33, 27.87) * mm});
            skArc(sketch, "E260", {"start": v(12.33, 27.87) * mm, "mid": v(10.74, 22.74) * mm, "end": v(9.78, 17.45) * mm});
            skArc(sketch, "E261", {"start": v(9.78, 17.45) * mm, "mid": v(9.57, 16.03) * mm, "end": v(9.78, 14.6) * mm});
            skArc(sketch, "E262", {"start": v(31.57, 57.36) * mm, "mid": v(30.31, 56.08) * mm, "end": v(29.7, 54.4) * mm});
            skArc(sketch, "E263", {"start": v(40.41, 59.57) * mm, "mid": v(35.76, 59.4) * mm, "end": v(31.57, 57.36) * mm});
            skArc(sketch, "E264", {"start": v(45.8, 56.99) * mm, "mid": v(43.34, 58.75) * mm, "end": v(40.41, 59.57) * mm});
            skArc(sketch, "E265", {"start": v(46.95, 55.24) * mm, "mid": v(46.49, 56.18) * mm, "end": v(45.8, 56.99) * mm});
            skArc(sketch, "E266", {"start": v(45.92, 55.24) * mm, "mid": v(46.43, 54.92) * mm, "end": v(46.95, 55.24) * mm});
            skArc(sketch, "E267", {"start": v(45.92, 55.24) * mm, "mid": v(44.31, 56.38) * mm, "end": v(42.44, 56.99) * mm});
            skArc(sketch, "E268", {"start": v(42.44, 56.99) * mm, "mid": v(39, 57.13) * mm, "end": v(35.6, 56.63) * mm});
            skArc(sketch, "E269", {"start": v(35.6, 56.63) * mm, "mid": v(33.3, 55.78) * mm, "end": v(31.16, 54.58) * mm});
            skArc(sketch, "E270", {"start": v(29.7, 54.4) * mm, "mid": v(30.45, 54.32) * mm, "end": v(31.16, 54.58) * mm});
            skSolve(sketch);
        }
        {
            var Q0;
            Q0 = qSketchRegion(id + "F6", true);
            extrude(context, id + "F7", {"entities" : qUnion([Q0]), "operationType" : NewBodyOperationType.REMOVE, "depth" : 10.16 * mm, "offsetDistance" : 25.4 * mm});
        }
        {
            var Q0;
            Q0=qCreatedBy(makeId("Front.planeOp"),FACE);
            var sketch = newSketch(context, id + "F8", { "sketchPlane" : qUnion([Q0])});
            skArc(sketch, "E271", {"start": v(22.58, 37.04) * mm, "mid": v(18.97, 31.7) * mm, "end": v(16.84, 25.62) * mm});
            skArc(sketch, "E272", {"start": v(30.72, 41.1) * mm, "mid": v(26.43, 39.53) * mm, "end": v(22.58, 37.04) * mm});
            skArc(sketch, "E273", {"start": v(30.72, 41.1) * mm, "mid": v(34.65, 42.6) * mm, "end": v(38.32, 44.63) * mm});
            skArc(sketch, "E274", {"start": v(43.1, 45.93) * mm, "mid": v(40.65, 45.5) * mm, "end": v(38.32, 44.63) * mm});
            skArc(sketch, "E275", {"start": v(39.74, 40.22) * mm, "mid": v(42.01, 42.72) * mm, "end": v(43.1, 45.93) * mm});
            skArc(sketch, "E276", {"start": v(33.96, 32.97) * mm, "mid": v(37.03, 36.45) * mm, "end": v(39.74, 40.22) * mm});
            skArc(sketch, "E277", {"start": v(25.48, 28.14) * mm, "mid": v(29.93, 30.18) * mm, "end": v(33.96, 32.97) * mm});
            skArc(sketch, "E278", {"start": v(20.44, 25.62) * mm, "mid": v(22.98, 26.85) * mm, "end": v(25.48, 28.14) * mm});
            skArc(sketch, "E279", {"start": v(17.49, 24.65) * mm, "mid": v(18.98, 25.09) * mm, "end": v(20.44, 25.62) * mm});
            skArc(sketch, "E280", {"start": v(16.84, 25.62) * mm, "mid": v(16.97, 25) * mm, "end": v(17.49, 24.65) * mm});
            skArc(sketch, "E281", {"start": v(-37.21, 43.61) * mm, "mid": v(-41.54, 46.17) * mm, "end": v(-46.43, 47.38) * mm});
            skArc(sketch, "E282", {"start": v(-26.53, 38.95) * mm, "mid": v(-31.65, 41.78) * mm, "end": v(-37.21, 43.61) * mm});
            skArc(sketch, "E283", {"start": v(-21.43, 31.04) * mm, "mid": v(-23.54, 35.28) * mm, "end": v(-26.53, 38.95) * mm});
            skArc(sketch, "E284", {"start": v(-20.17, 26.75) * mm, "mid": v(-20.55, 28.97) * mm, "end": v(-21.43, 31.04) * mm});
            skArc(sketch, "E285", {"start": v(-22.96, 26.75) * mm, "mid": v(-21.57, 26.07) * mm, "end": v(-20.17, 26.75) * mm});
            skArc(sketch, "E286", {"start": v(-30.46, 30.5) * mm, "mid": v(-26.73, 28.59) * mm, "end": v(-22.96, 26.75) * mm});
            skArc(sketch, "E287", {"start": v(-35.69, 32.97) * mm, "mid": v(-33.22, 31.44) * mm, "end": v(-30.46, 30.5) * mm});
            skArc(sketch, "E288", {"start": v(-41.54, 38.95) * mm, "mid": v(-38.84, 35.74) * mm, "end": v(-35.69, 32.97) * mm});
            skArc(sketch, "E289", {"start": v(-41.54, 38.95) * mm, "mid": v(-43.3, 41.62) * mm, "end": v(-45.13, 44.24) * mm});
            skArc(sketch, "E290", {"start": v(-46.43, 47.38) * mm, "mid": v(-46.23, 45.62) * mm, "end": v(-45.13, 44.24) * mm});
            skSolve(sketch);
        }
        {
            var Q0;
            Q0=makeQuery(id+"F8.imprint","IMPRINT",FACE,{"disambiguationData":[TD([[makeQuery(id+"F8.imprint","IMPRINT",EDGE,{"derivedFrom":sQuery(id+"F8.wireOp",EDGE,"E281")}),1.0]])]});
            var Q1;
            Q1=makeQuery(id+"F8.imprint","IMPRINT",FACE,{"disambiguationData":[TD([[makeQuery(id+"F8.imprint","IMPRINT",EDGE,{"derivedFrom":sQuery(id+"F8.wireOp",EDGE,"E271")}),1.0]])]});
            extrude(context, id + "F9", {"entities" : qUnion([Q0, Q1]), "depth" : 10.16 * mm, "offsetDistance" : 25.4 * mm});
        }
        {
            var Q0;
            Q0=qCreatedBy(makeId("Front.planeOp"),FACE);
            var sketch = newSketch(context, id + "F10", { "sketchPlane" : qUnion([Q0])});
            skLineSegment(sketch, "E291.bottom", {"start": v(-79.84, 91.67) * mm, "end": v(72.56, 91.67) * mm});
            skLineSegment(sketch, "E291.top", {"start": v(-79.84, -86.13) * mm, "end": v(72.56, -86.13) * mm});
            skLineSegment(sketch, "E291.left", {"start": v(-79.84, 91.67) * mm, "end": v(-79.84, -86.13) * mm});
            skLineSegment(sketch, "E291.right", {"start": v(72.56, 91.67) * mm, "end": v(72.56, -86.13) * mm});
            skSolve(sketch);
        }
        {
            var Q0;
            Q0=makeQuery(id+"F10.imprint","IMPRINT",FACE,{"disambiguationData":[TD([[makeQuery(id+"F10.imprint","IMPRINT",EDGE,{"derivedFrom":sQuery(id+"F10.wireOp",EDGE,"E291.bottom")}),-1.0]])]});
            extrude(context, id + "F11", {"entities" : qUnion([Q0]), "depth" : 2.54 * mm, "offsetDistance" : 25.4 * mm});
        }
    });
